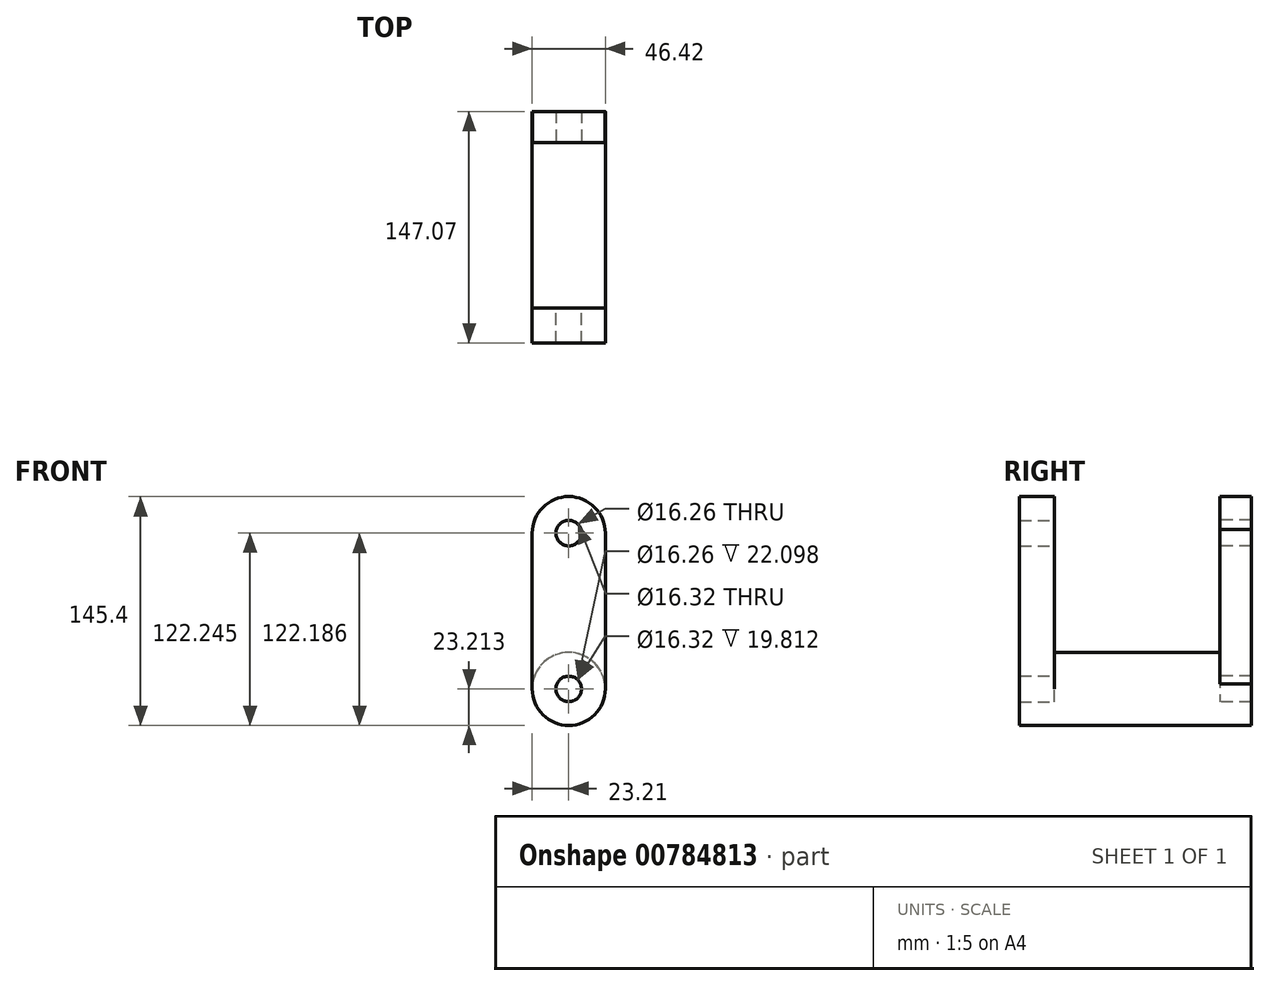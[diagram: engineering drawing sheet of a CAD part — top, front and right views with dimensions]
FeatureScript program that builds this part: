
annotation { "Feature Type Name" : "Feature", "Feature Type Description" : "" }
export const myFeature = defineFeature(function(context is Context, id is Id, definition is map)
    precondition{}
    {
        {
            var Q0;
            Q0=qCreatedBy(makeId("Front.planeOp"),FACE);
            var sketch = newSketch(context, id + "F0", { "sketchPlane" : qUnion([Q0])});
            skCircle(sketch, "E0", {"center": v(25.79, -54.89) * mm, "radius": 23.21 * mm});
            skSolve(sketch);
        }
        {
            var Q0;
            Q0=makeQuery(id+"F0.imprint","IMPRINT",FACE,{"disambiguationData":[TD([[makeQuery(id+"F0.imprint","IMPRINT",EDGE,{"derivedFrom":sQuery(id+"F0.wireOp",EDGE,"E0")}),1.0]])]});
            extrude(context, id + "F1", {"entities" : qUnion([Q0]), "oppositeDirection" : true, "depth" : 105.16 * mm, "offsetDistance" : 25.4 * mm});
        }
        {
            var Q0;
            Q0=makeQuery(id+"F1.opExtrude","CAP_FACE",FACE,{"disambiguationData":[OSD([sQuery(id+"F0.wireOp",EDGE,"E0")])],"isStart":true});
            var sketch = newSketch(context, id + "F2", { "sketchPlane" : qUnion([Q0])});
            skCircle(sketch, "E1", {"center": v(25.79, -54.89) * mm, "radius": 8.13 * mm});
            skLineSegment(sketch, "E2", {"start": v(2.58, -54.89) * mm, "end": v(2.58, 44.09) * mm});
            skLineSegment(sketch, "E3", {"start": v(49, -54.89) * mm, "end": v(49, 44.09) * mm});
            skArc(sketch, "E4", {"start": v(49, 44.09) * mm, "mid": v(25.79, 67.3) * mm, "end": v(2.58, 44.09) * mm});
            skCircle(sketch, "E5", {"center": v(25.79, 44.09) * mm, "radius": 8.13 * mm});
            skSolve(sketch);
        }
        {
            var Q0;
            {var subQ1=sQuery(id+"F2.wireOp",EDGE,"E2");Q0=makeQuery(id+"F2.imprint","IMPRINT",FACE,{"disambiguationData":[TD([[makeQuery(id+"F2.imprint","IMPRINT",EDGE,{"derivedFrom":subQ1}),-1.0]])]});}
            var Q1;
            Q1=makeQuery(id+"F2.imprint","IMPRINT",FACE,{"disambiguationData":[TD([[makeQuery(id+"F2.imprint","IMPRINT",EDGE,{"derivedFrom":sQuery(id+"F2.wireOp",EDGE,"E1")}),-1.0]])]});
            extrude(context, id + "F3", {"entities" : qUnion([Q0, Q1]), "operationType" : NewBodyOperationType.ADD, "depth" : 22.1 * mm, "offsetDistance" : 25.4 * mm});
        }
        {
            var Q0;
            Q0=makeQuery(id+"F1.opExtrude","CAP_FACE",FACE,{"disambiguationData":[OSD([sQuery(id+"F0.wireOp",EDGE,"E0")])],"isStart":false});
            var sketch = newSketch(context, id + "F4", { "sketchPlane" : qUnion([Q0])});
            skLineSegment(sketch, "E6", {"start": v(-48.78, -51.67) * mm, "end": v(-48.78, 46.48) * mm});
            skLineSegment(sketch, "E7", {"start": v(-2.8, -51.67) * mm, "end": v(-2.8, 46.48) * mm});
            skArc(sketch, "E8", {"start": v(-2.8, 46.48) * mm, "mid": v(-25.79, 67.25) * mm, "end": v(-48.78, 46.48) * mm});
            skCircle(sketch, "E9", {"center": v(-25.79, 44.14) * mm, "radius": 8.16 * mm});
            skCircle(sketch, "E10", {"center": v(-25.79, -54.89) * mm, "radius": 8.16 * mm});
            skSolve(sketch);
        }
        {
            var Q0;
            {var subQ1=sQuery(id+"F4.wireOp",EDGE,"E6");Q0=makeQuery(id+"F4.imprint","IMPRINT",FACE,{"disambiguationData":[TD([[makeQuery(id+"F4.imprint","IMPRINT",EDGE,{"derivedFrom":subQ1}),-1.0]])]});}
            var Q1;
            Q1=makeQuery(id+"F4.imprint","IMPRINT",FACE,{"disambiguationData":[TD([[makeQuery(id+"F4.imprint","IMPRINT",EDGE,{"derivedFrom":sQuery(id+"F4.wireOp",EDGE,"E10")}),-1.0]])]});
            extrude(context, id + "F5", {"entities" : qUnion([Q0, Q1]), "operationType" : NewBodyOperationType.ADD, "depth" : 19.8 * mm, "offsetDistance" : 25.4 * mm});
        }
    });
